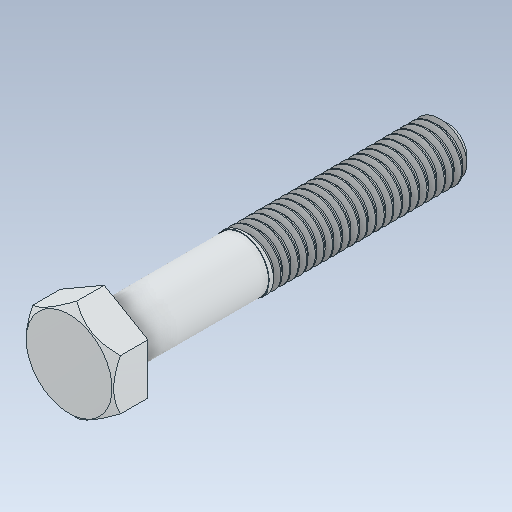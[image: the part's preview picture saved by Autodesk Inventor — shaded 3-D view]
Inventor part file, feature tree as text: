
AUTODESK INVENTOR PART (.ipt)
format: ipt  version: 2021 (Build 250183000, 183)  size: 1,050,624 bytes
history: mixed  units: in
note: dims shown in document units (in); Inventor stores cm internally (conversion verified against a paired STEP export)
features: fillet x1, imported_body x1
ambient origin geometry x8: Origin, YZ Plane, XZ Plane, XY Plane, X Axis, Y Axis, Z Axis, Center Point
bodies: Solid1 (imported_parasolid)
feature tree (2):
  fillet  "Fillet1"  [1 undecoded]
  imported_body  NMx_Import_Brep_tag  [imported B-rep: ~5 faces, bbox_mm=None]
note: 1 required parameter value undecoded (feature->parameter linkage not recoverable at this tier; creation-order binding heuristic only, values carry confidence <= 0.55)
